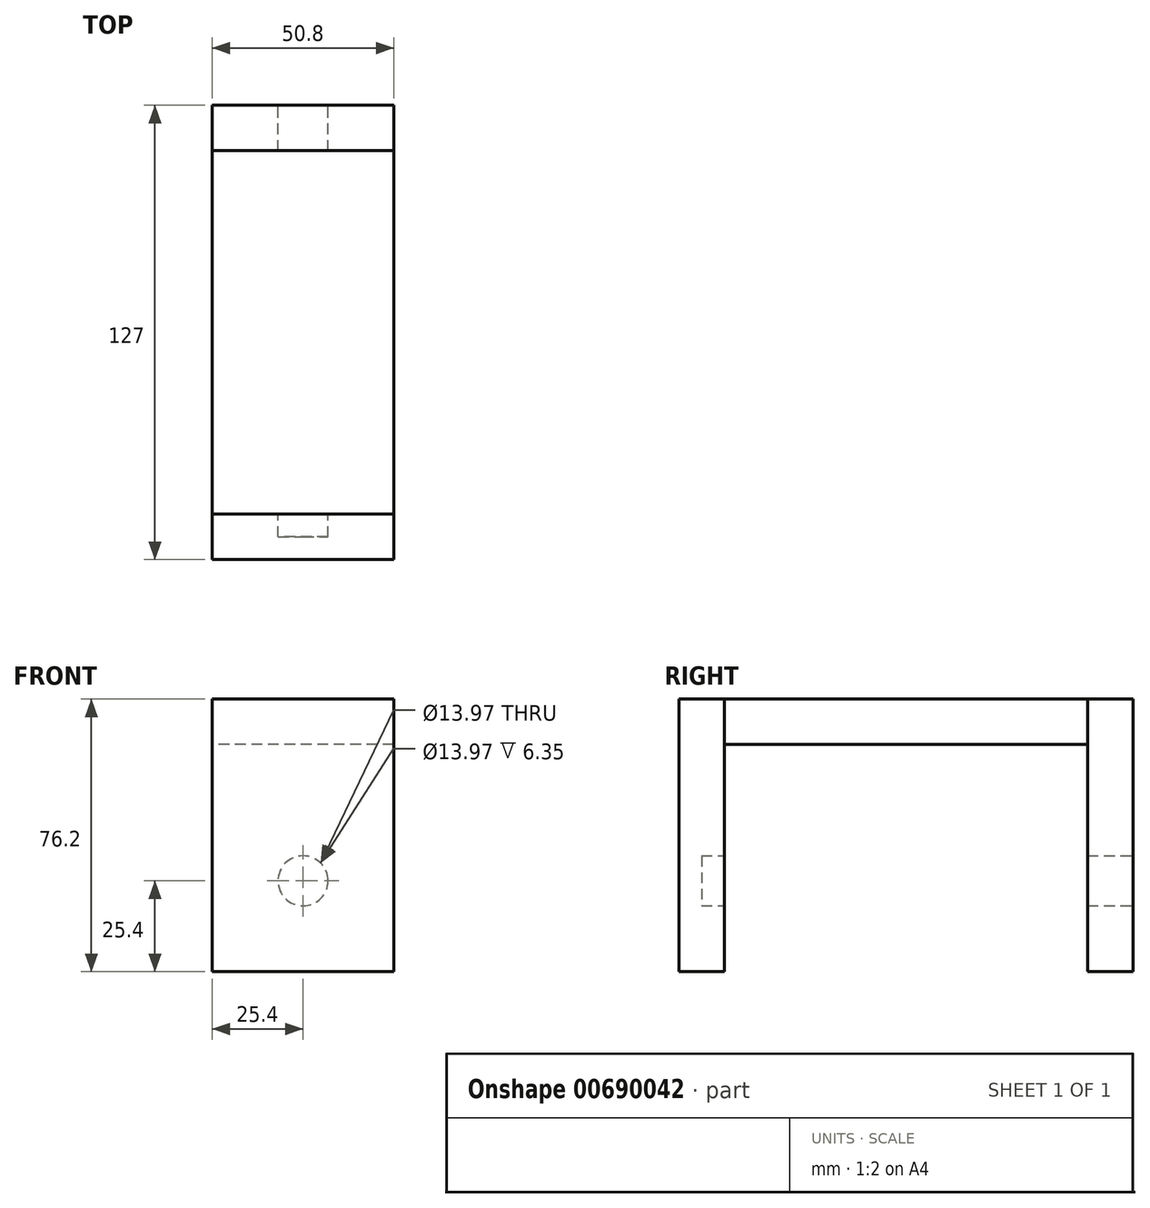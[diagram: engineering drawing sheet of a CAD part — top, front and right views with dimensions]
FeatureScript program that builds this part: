
annotation { "Feature Type Name" : "Feature", "Feature Type Description" : "" }
export const myFeature = defineFeature(function(context is Context, id is Id, definition is map)
    precondition{}
    {
        {
            var Q0;
            Q0=qCreatedBy(makeId("Top.planeOp"),FACE);
            var sketch = newSketch(context, id + "F0", { "sketchPlane" : qUnion([Q0])});
            skLineSegment(sketch, "E0.bottom", {"start": v(25.4, 50.8) * mm, "end": v(-25.4, 50.8) * mm});
            skLineSegment(sketch, "E0.top", {"start": v(25.4, -50.8) * mm, "end": v(-25.4, -50.8) * mm});
            skLineSegment(sketch, "E0.left", {"start": v(25.4, 50.8) * mm, "end": v(25.4, -50.8) * mm});
            skLineSegment(sketch, "E0.right", {"start": v(-25.4, 50.8) * mm, "end": v(-25.4, -50.8) * mm});
            skPoint(sketch, "E0.middle", {"position": v(0, 0) * mm});
            skSolve(sketch);
        }
        {
            var Q0;
            Q0 = qSketchRegion(id + "F0", true);
            extrude(context, id + "F1", {"entities" : qUnion([Q0]), "depth" : 12.7 * mm, "offsetDistance" : 25.4 * mm});
        }
        {
            var Q0;
            Q0=makeQuery(id+"F1.opExtrude","CAP_FACE",FACE,{"disambiguationData":[OSD([sQuery(id+"F0.wireOp",EDGE,"E0.bottom"),sQuery(id+"F0.wireOp",EDGE,"E0.top"),sQuery(id+"F0.wireOp",EDGE,"E0.left"),sQuery(id+"F0.wireOp",EDGE,"E0.right")])],"isStart":false});
            var sketch = newSketch(context, id + "F2", { "sketchPlane" : qUnion([Q0])});
            skLineSegment(sketch, "E1.bottom", {"start": v(-25.4, 50.8) * mm, "end": v(25.4, 50.8) * mm});
            skLineSegment(sketch, "E1.top", {"start": v(-25.4, 63.5) * mm, "end": v(25.4, 63.5) * mm});
            skLineSegment(sketch, "E1.left", {"start": v(-25.4, 50.8) * mm, "end": v(-25.4, 63.5) * mm});
            skLineSegment(sketch, "E1.right", {"start": v(25.4, 50.8) * mm, "end": v(25.4, 63.5) * mm});
            skLineSegment(sketch, "E2.bottom", {"start": v(-25.4, -50.8) * mm, "end": v(25.4, -50.8) * mm});
            skLineSegment(sketch, "E2.top", {"start": v(-25.4, -63.5) * mm, "end": v(25.4, -63.5) * mm});
            skLineSegment(sketch, "E2.left", {"start": v(-25.4, -50.8) * mm, "end": v(-25.4, -63.5) * mm});
            skLineSegment(sketch, "E2.right", {"start": v(25.4, -50.8) * mm, "end": v(25.4, -63.5) * mm});
            skSolve(sketch);
        }
        {
            var Q0;
            Q0 = qSketchRegion(id + "F2", true);
            extrude(context, id + "F3", {"entities" : qUnion([Q0]), "oppositeDirection" : true, "depth" : 76.2 * mm, "offsetDistance" : 25.4 * mm});
        }
        {
            var Q0;
            Q0=makeQuery(id+"F3.opExtrude","SWEPT_FACE",FACE,{"disambiguationData":[OSD([sQuery(id+"F2.wireOp",EDGE,"E1.top")])]});
            var sketch = newSketch(context, id + "F4", { "sketchPlane" : qUnion([Q0])});
            skCircle(sketch, "E3", {"center": v(0, -38.1) * mm, "radius": 6.99 * mm});
            skLineSegment(sketch, "E4", {"start": v(0, -38.1) * mm, "end": v(0, -63.5) * mm});
            skSolve(sketch);
        }
        {
            var Q0;
            Q0=makeQuery(id+"F4.imprint","IMPRINT",FACE,{"disambiguationData":[TD([[makeQuery(id+"F4.imprint","IMPRINT",EDGE,{"derivedFrom":sQuery(id+"F4.wireOp",EDGE,"E3")}),1.0]])]});
            extrude(context, id + "F5", {"entities" : qUnion([Q0]), "operationType" : NewBodyOperationType.REMOVE, "oppositeDirection" : true, "depth" : 120.65 * mm, "offsetDistance" : 25.4 * mm});
        }
    });
